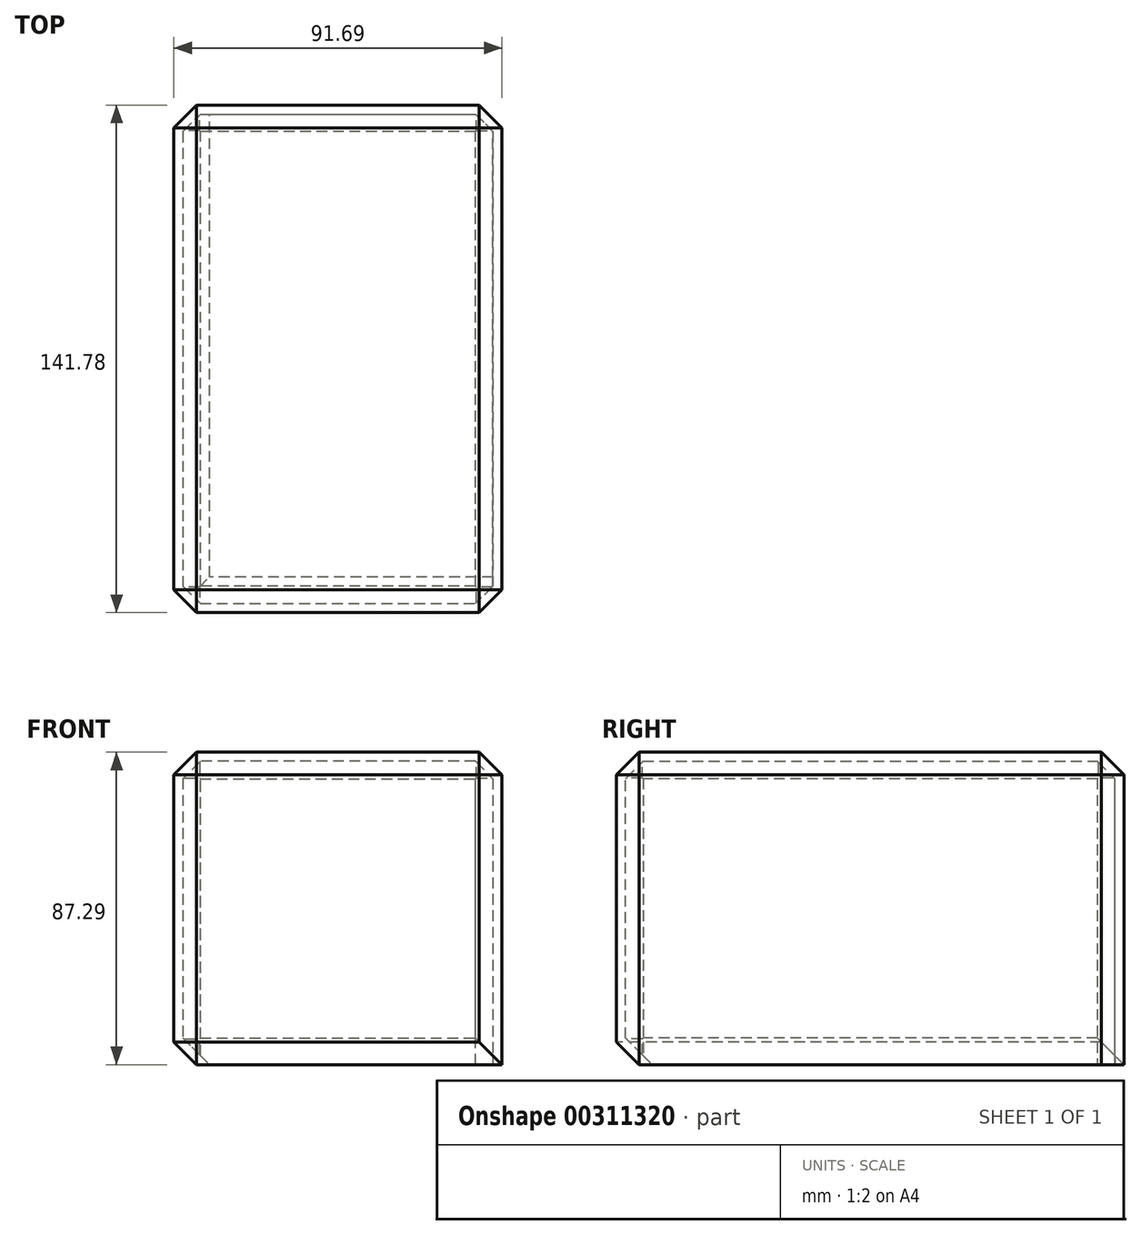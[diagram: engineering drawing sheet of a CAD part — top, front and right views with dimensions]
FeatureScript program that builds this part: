
annotation { "Feature Type Name" : "Feature", "Feature Type Description" : "" }
export const myFeature = defineFeature(function(context is Context, id is Id, definition is map)
    precondition{}
    {
        {
            var Q0;
            Q0=qCreatedBy(makeId("Front.planeOp"),FACE);
            var sketch = newSketch(context, id + "F0", { "sketchPlane" : qUnion([Q0])});
            skLineSegment(sketch, "E0.bottom", {"start": v(-91.69, -87.29) * mm, "end": v(0, -87.29) * mm});
            skLineSegment(sketch, "E0.top", {"start": v(-91.69, 0) * mm, "end": v(0, 0) * mm});
            skLineSegment(sketch, "E0.left", {"start": v(-91.69, -87.29) * mm, "end": v(-91.69, 0) * mm});
            skLineSegment(sketch, "E0.right", {"start": v(0, -87.29) * mm, "end": v(0, 0) * mm});
            skSolve(sketch);
        }
        {
            var Q0;
            Q0=makeQuery(id+"F0.imprint","IMPRINT",FACE,{"disambiguationData":[TD([[makeQuery(id+"F0.imprint","IMPRINT",EDGE,{"derivedFrom":sQuery(id+"F0.wireOp",EDGE,"E0.bottom")}),1.0]])]});
            extrude(context, id + "F1", {"entities" : qUnion([Q0]), "depth" : 141.78 * mm});
        }
        {
            var Q0;
            Q0=makeQuery(id+"F1.opExtrude","CAP_EDGE",EDGE,{"disambiguationData":[OSD([sQuery(id+"F0.wireOp",EDGE,"E0.top")])],"isStart":false});
            var Q1;
            Q1=makeQuery(id+"F1.opExtrude","SWEPT_FACE",FACE,{"disambiguationData":[OSD([sQuery(id+"F0.wireOp",EDGE,"E0.left")])]});
            var Q2;
            Q2=makeQuery(id+"F1.opExtrude","SWEPT_FACE",FACE,{"disambiguationData":[OSD([sQuery(id+"F0.wireOp",EDGE,"E0.top")])]});
            var Q3;
            Q3=makeQuery(id+"F1.opExtrude","CAP_FACE",FACE,{"disambiguationData":[OSD([sQuery(id+"F0.wireOp",EDGE,"E0.bottom"),sQuery(id+"F0.wireOp",EDGE,"E0.top"),sQuery(id+"F0.wireOp",EDGE,"E0.left"),sQuery(id+"F0.wireOp",EDGE,"E0.right")])],"isStart":false});
            var Q4;
            Q4=makeQuery(id+"F1.opExtrude","CAP_EDGE",EDGE,{"disambiguationData":[OSD([sQuery(id+"F0.wireOp",EDGE,"E0.right")])],"isStart":true});
            chamfer(context, id + "F2", {"entities" : qUnion([Q0, Q1, Q2, Q3, Q4]), "width" : 6.35 * mm, "tangentPropagation" : true});
        }
        {
            var Q0;
            Q0=makeQuery(id+"F1.opExtrude","SWEPT_FACE",FACE,{"disambiguationData":[OSD([sQuery(id+"F0.wireOp",EDGE,"E0.bottom")])]});
            shell(context, id + "F3", {"entities" : qUnion([Q0]), "thickness" : 2.54 * mm});
        }
    });
